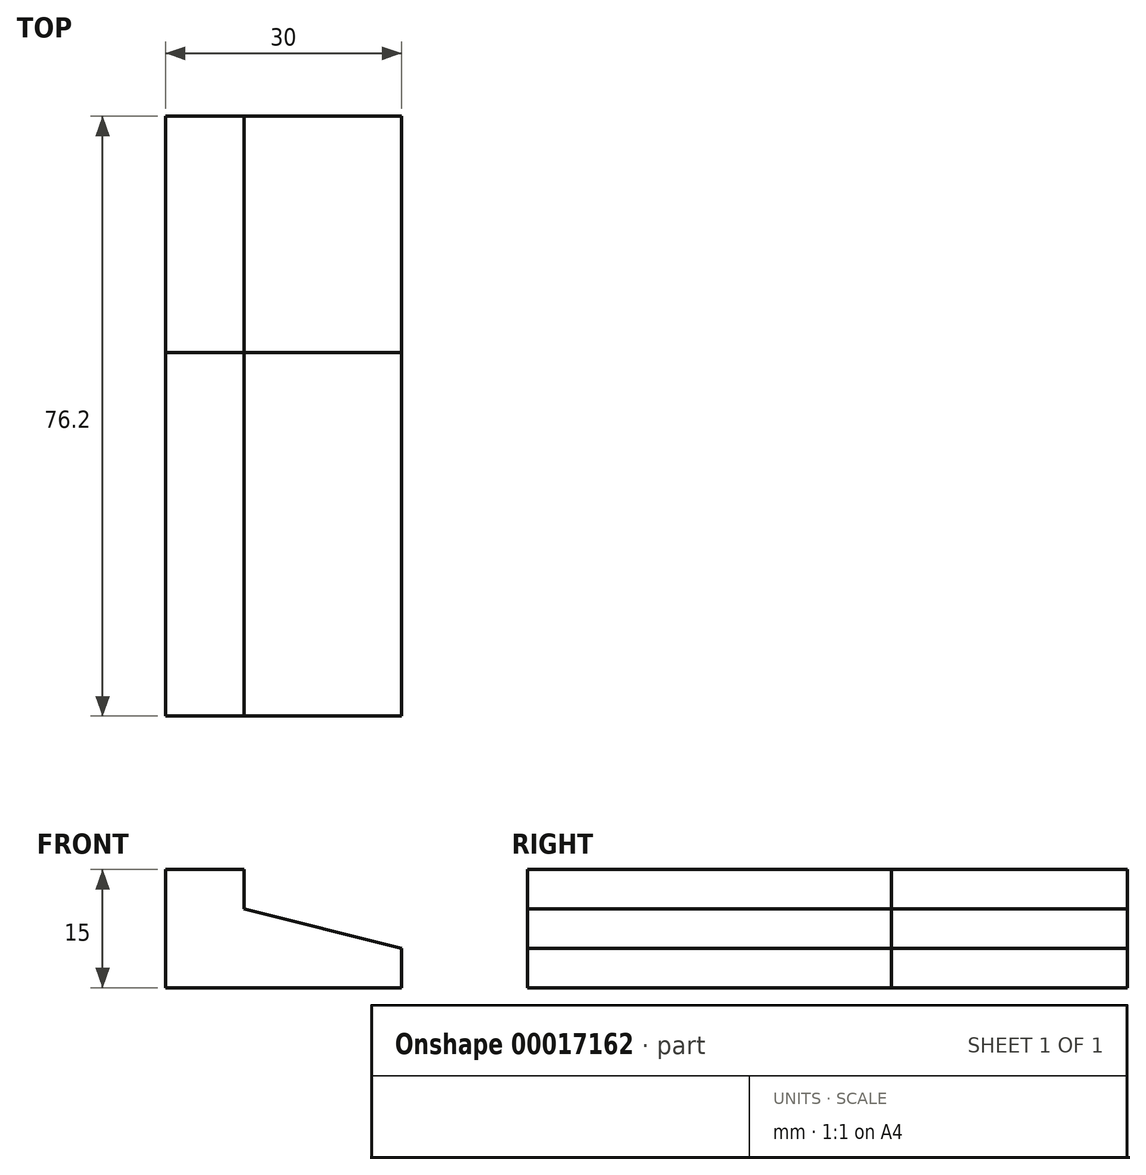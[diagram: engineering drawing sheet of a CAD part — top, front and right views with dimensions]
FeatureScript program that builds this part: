
annotation { "Feature Type Name" : "Feature", "Feature Type Description" : "" }
export const myFeature = defineFeature(function(context is Context, id is Id, definition is map)
    precondition{}
    {
        {
            var Q0;
            Q0=qCreatedBy(makeId("Front.planeOp"),FACE);
            var sketch = newSketch(context, id + "F0", { "sketchPlane" : qUnion([Q0])});
            skLineSegment(sketch, "E0", {"start": v(-27.7, 10) * mm, "end": v(-27.7, -5) * mm});
            skLineSegment(sketch, "E1", {"start": v(-27.7, -5) * mm, "end": v(2.3, -5) * mm});
            skLineSegment(sketch, "E2", {"start": v(2.3, -5) * mm, "end": v(2.3, 0) * mm});
            skLineSegment(sketch, "E3", {"start": v(2.3, 0) * mm, "end": v(-17.7, 5) * mm});
            skLineSegment(sketch, "E4", {"start": v(-17.7, 5) * mm, "end": v(-17.7, 10) * mm});
            skLineSegment(sketch, "E5", {"start": v(-17.7, 10) * mm, "end": v(-27.7, 10) * mm});
            skSolve(sketch);
        }
        {
            var Q0;
            Q0=makeQuery(id+"F0.imprint","IMPRINT",FACE,{"disambiguationData":[TD([[makeQuery(id+"F0.imprint","IMPRINT",EDGE,{"derivedFrom":sQuery(id+"F0.wireOp",EDGE,"E0")}),1.0]])]});
            extrude(context, id + "F1", {"entities" : qUnion([Q0]), "depth" : 30 * mm});
        }
        {
            var Q0;
            Q0=makeQuery(id+"F0.imprint","IMPRINT",FACE,{"disambiguationData":[TD([[makeQuery(id+"F0.imprint","IMPRINT",EDGE,{"derivedFrom":sQuery(id+"F0.wireOp",EDGE,"E0")}),1.0]])]});
            extrude(context, id + "F2", {"entities" : qUnion([Q0]), "depth" : 76.2 * mm});
        }
    });
